# Revit family: Seating_Inc-Monterey_ll_High_Back_Task
name_source: partatom
category: Furniture
revit_build: Autodesk Revit 2014 (Build: 20130308_1515(x64)
units: mm (PartAtom-declared; Revit-internal decimal feet)

## types (3) — shared parameters
Aluminum Finish = STI - Aluminum
Arm Finish = STI - Plastic Black
Assembly Code = E2020200
Back Finish = STI - Leather
Base Finish = STI - Plastic Black
Caster Finish = STI - Plastic Black
Depth = 24 1/2"
Front Finish = STI - Leather
Hardware Finish = STI - Plastic Black
Height = 38"
Keynote = 12500
Low Emitting Finish = Yes
Low Emitting Material = Yes
Manufacturer = Seating Inc
Plastic Finish = STI - Plastic Black
Salvage or Reuse = Yes
Seat Finish = STI - Leather
Type Comments = Quick Configuration
URL = www.seatinginc.com
Width = 24 1/2"
zero-valued in all types: Percentage of Recycled Content

## per-type parameters (varying)
| type | Control A | Control B | Control C | Description | Seat Dist | Seat L Dist |
| Q-3MOHB-A | Yes | No | No | Monterey II High Back Task Basic Model 24.5W x 24.5D x 38H | 19 11/16" | 14 1/2" |
| Q-3MOHB-B | No | Yes | No | Monterey II High Back Task Value Packed 24.5W x 24.5D x 38H | 20 29/32" | 15 1/16" |
| Q-3MOHB-C | No | No | Yes | Monterey II High Back Task Fully Loaded 24.5W x 24.5D x 38H | 21 11/16" | 15" |

note: column(s) folded — value = type name in every type: Model

## geometry (parser evidence)
native form markers: Sweep x5
no freeform markers — native parametric forms only
